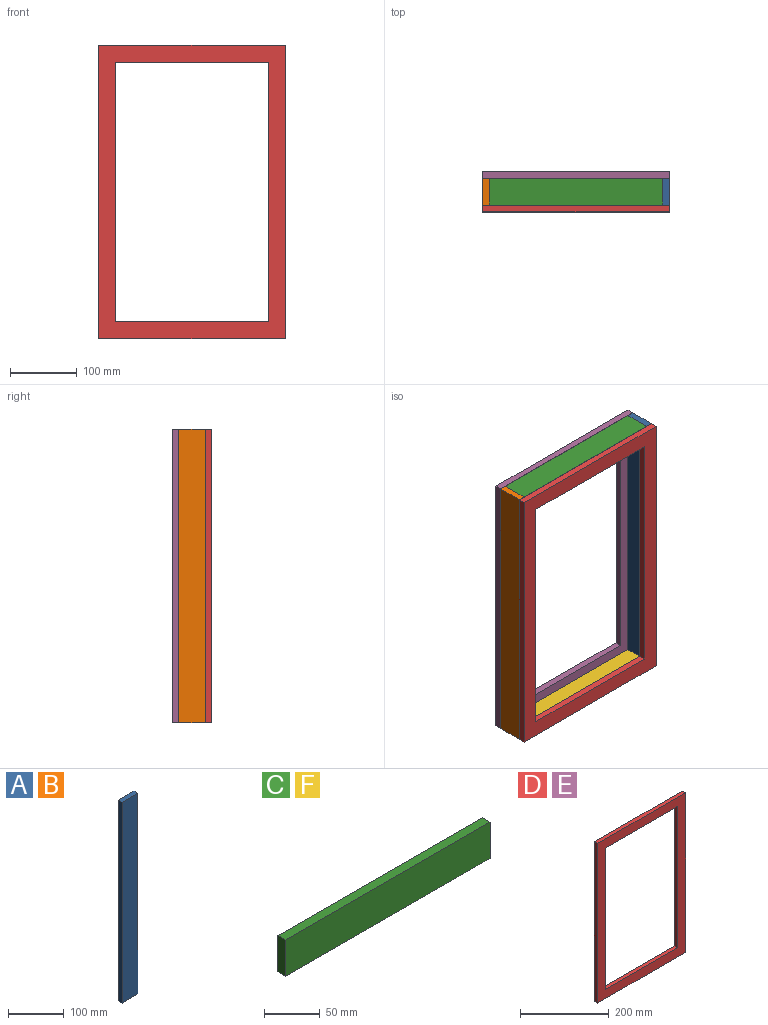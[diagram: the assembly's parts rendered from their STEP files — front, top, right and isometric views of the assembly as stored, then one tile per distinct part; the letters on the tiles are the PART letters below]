
ASSEMBLY  parts=6 mates=5
PART A: 6 faces, bbox 40x10x440 mm
  f0: plane 40x10mm, normal (0,0,-1), area 400mm2, adj f1,f3,f4,f5
  f1: plane 440x10mm, normal (1,0,0), area 4400mm2, adj f0,f2,f4,f5
  f2: plane 40x10mm, normal (0,0,1), area 400mm2, adj f1,f3,f4,f5
  f3: plane 440x10mm, normal (-1,0,0), area 4400mm2, adj f0,f2,f4,f5
  f4: plane 440x40mm, normal (0,-1,0), area 17600mm2, adj f0,f1,f2,f3
  f5: plane 440x40mm, normal (0,1,0), area 17600mm2, adj f0,f1,f2,f3
PART B: same geometry as A
PART C: 6 faces, bbox 260x10x40 mm
  f0: plane 260x10mm, normal (0,0,-1), area 2600mm2, adj f1,f3,f4,f5
  f1: plane 40x10mm, normal (1,0,0), area 400mm2, adj f0,f2,f4,f5
  f2: plane 260x10mm, normal (0,0,1), area 2600mm2, adj f1,f3,f4,f5
  f3: plane 40x10mm, normal (-1,0,0), area 400mm2, adj f0,f2,f4,f5
  f4: plane 260x40mm, normal (0,-1,0), area 10400mm2, adj f0,f1,f2,f3
  f5: plane 260x40mm, normal (0,1,0), area 10400mm2, adj f0,f1,f2,f3
PART D: 10 faces, bbox 280x10x440 mm
  f0: plane 280x10mm, normal (0,0,-1), area 2800mm2, adj f1,f7,f8,f9
  f1: plane 440x10mm, normal (1,0,0), area 4400mm2, adj f0,f2,f8,f9
  f2: plane 280x10mm, normal (0,0,1), area 2800mm2, adj f1,f7,f8,f9
  f3: plane 390x10mm, normal (-1,0,0), area 3900mm2, adj f4,f6,f8,f9
  f4: plane 230x10mm, normal (0,0,1), area 2300mm2, adj f3,f5,f8,f9
  f5: plane 390x10mm, normal (1,0,0), area 3900mm2, adj f4,f6,f8,f9
  f6: plane 230x10mm, normal (0,0,-1), area 2300mm2, adj f3,f5,f8,f9
  f7: plane 440x10mm, normal (-1,0,0), area 4400mm2, adj f0,f2,f8,f9
  f8: plane 440x280mm, normal (0,-1,0), area 33500mm2, adj f0,f1,f2,f3,f4,f5,f6,f7
  f9: plane 440x280mm, normal (0,1,0), area 33500mm2, adj f0,f1,f2,f3,f4,f5,f6,f7
PART E: same geometry as D
PART F: same geometry as C
PLACE A rot(axis=(0,0,-1),90deg) t=(421.49,113.15,-36.55)mm
PLACE B rot(axis=(0,0,-1),90deg) t=(151.49,113.15,-36.55)mm
PLACE C rot(axis=(-1,0,0),90deg) t=(281.49,113.15,173.45)mm
PLACE D t=(281.49,93.15,-45.81)mm
PLACE E t=(281.49,143.15,-45.81)mm
PLACE F rot(axis=(-1,0,0),90deg) t=(281.49,113.15,-256.55)mm
MATE fastened A.f3 <-> E.f8  axis (0,1,0) through (421.49,133.15,183.45)mm
MATE fastened D.f9 <-> C.f0  axis (0,1,0) through (281.49,93.15,183.45)mm
MATE fastened B.f3 <-> E.f8  axis (0,1,0) through (141.49,133.15,183.45)mm
MATE fastened C.f3 <-> B.f5  axis (-1,0,0) through (151.49,133.15,183.45)mm
MATE fastened F.f1 <-> A.f4  axis (1,0,0) through (411.49,133.15,-256.55)mm
